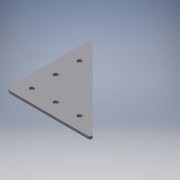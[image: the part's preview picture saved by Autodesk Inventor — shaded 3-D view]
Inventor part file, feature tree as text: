
AUTODESK INVENTOR PART (.ipt)
format: ipt  version: 2017 (Build 210142000, 142)  size: 350,720 bytes
history: native  units: mm
features: sketch x2, extrude x1, hole x1, projected_geometry x1
ambient origin geometry x8: Origin, YZ Plane, XZ Plane, XY Plane, X Axis, Y Axis, Z Axis, Center Point
bodies: Solid1 (feature_tree)
feature tree (5):
  extrude  "Extrusion1"  [1 undecoded]
  hole  "Hole1"  [1 undecoded]
  sketch  "Sketch1"  dims[d0=3.0mm d1=0.0mm]
  sketch  "Sketch2"  dims[d2=5.2mm d3=6.0mm d4=4.0mm d5=2.0mm d6=90.0deg d7=8.0mm d8=20.594885mm]
  projected_geometry  "Projected Loop1"
note: 2 required parameter values undecoded (feature->parameter linkage not recoverable at this tier; creation-order binding heuristic only, values carry confidence <= 0.55)
